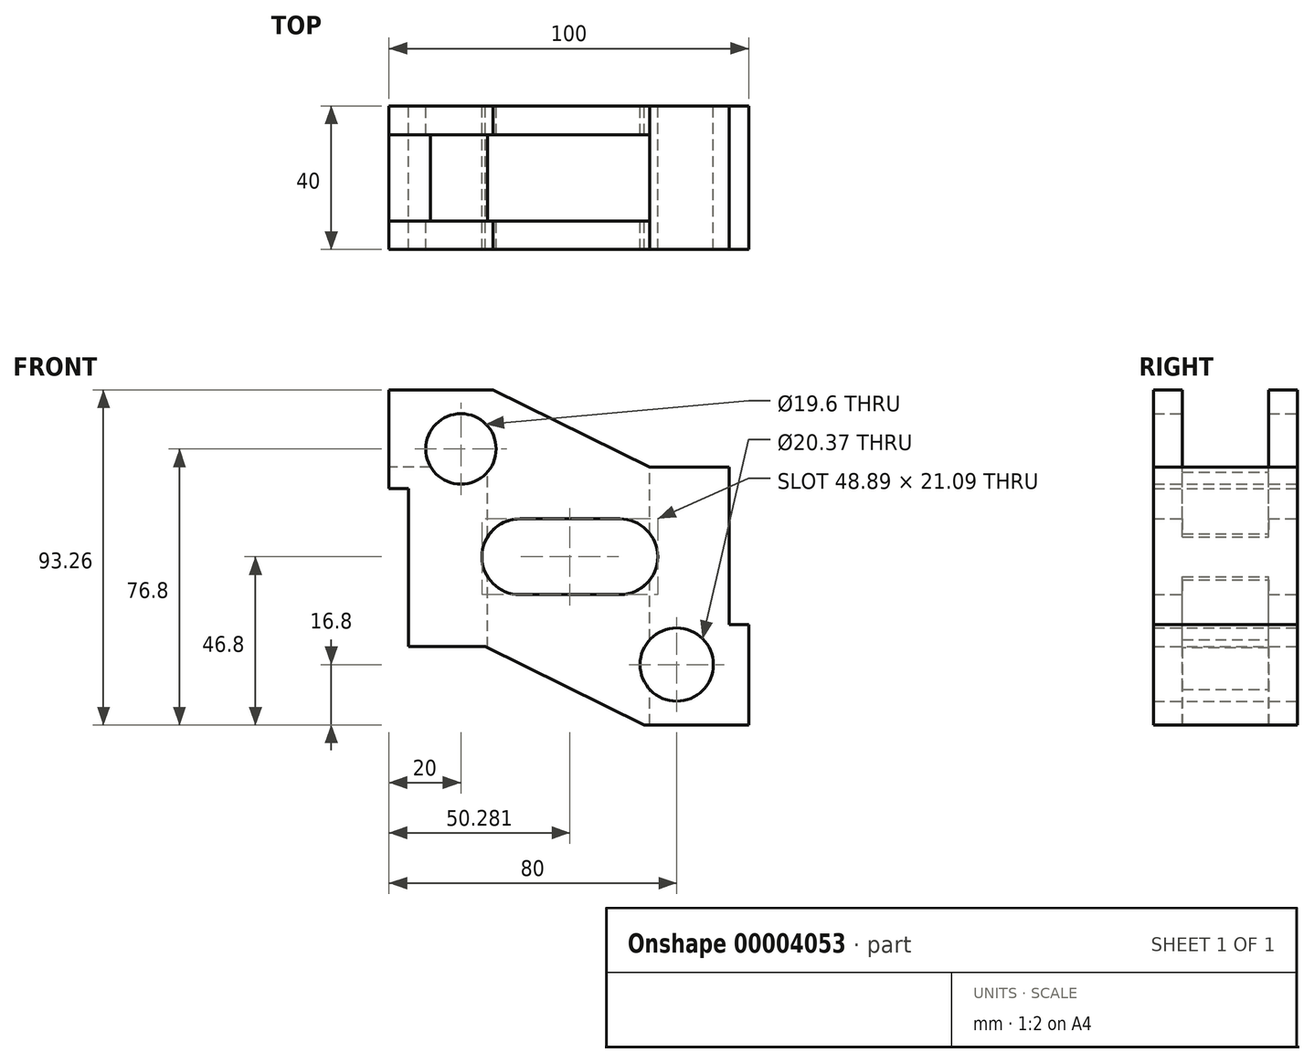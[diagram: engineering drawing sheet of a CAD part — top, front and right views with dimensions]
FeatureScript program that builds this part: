
annotation { "Feature Type Name" : "Feature", "Feature Type Description" : "" }
export const myFeature = defineFeature(function(context is Context, id is Id, definition is map)
    precondition{}
    {
        {
            var Q0;
            Q0=qCreatedBy(makeId("Front.planeOp"),FACE);
            var sketch = newSketch(context, id + "F0", { "sketchPlane" : qUnion([Q0])});
            skLineSegment(sketch, "E0", {"start": v(-50, 18.93) * mm, "end": v(-50, 46.46) * mm});
            skLineSegment(sketch, "E1", {"start": v(-50, 46.46) * mm, "end": v(-21.02, 46.46) * mm});
            skLineSegment(sketch, "E2", {"start": v(-21.02, 46.46) * mm, "end": v(22.51, 25) * mm});
            skLineSegment(sketch, "E3", {"start": v(22.51, 25) * mm, "end": v(44.58, 25) * mm});
            skLineSegment(sketch, "E4", {"start": v(50, -18.93) * mm, "end": v(50, -46.8) * mm});
            skLineSegment(sketch, "E5", {"start": v(50, -46.8) * mm, "end": v(21.02, -46.8) * mm});
            skLineSegment(sketch, "E6", {"start": v(21.02, -46.8) * mm, "end": v(-23.2, -25) * mm});
            skLineSegment(sketch, "E7", {"start": v(-23.2, -25) * mm, "end": v(-44.58, -25) * mm});
            skCircle(sketch, "E8", {"center": v(-30, 30) * mm, "radius": 9.8 * mm});
            skCircle(sketch, "E9", {"center": v(30, -30) * mm, "radius": 10.19 * mm});
            skLineSegment(sketch, "E10", {"start": v(-50, 18.93) * mm, "end": v(-44.58, 18.93) * mm});
            skLineSegment(sketch, "E11", {"start": v(-44.58, 18.93) * mm, "end": v(-44.58, -25) * mm});
            skLineSegment(sketch, "E12", {"start": v(44.58, 25) * mm, "end": v(44.58, -18.93) * mm});
            skLineSegment(sketch, "E13", {"start": v(44.58, -18.93) * mm, "end": v(50, -18.93) * mm});
            skArc(sketch, "E14", {"start": v(-13.62, 10.55) * mm, "mid": v(-24.16, 0) * mm, "end": v(-13.62, -10.55) * mm});
            skArc(sketch, "E15", {"start": v(14.18, -10.55) * mm, "mid": v(24.72, 0) * mm, "end": v(14.18, 10.55) * mm});
            skLineSegment(sketch, "E16", {"start": v(-13.62, 10.55) * mm, "end": v(14.18, 10.55) * mm});
            skLineSegment(sketch, "E17", {"start": v(-13.62, -10.55) * mm, "end": v(14.18, -10.55) * mm});
            skSolve(sketch);
        }
        {
            var Q0;
            Q0 = qSketchRegion(id + "F0", true);
            extrude(context, id + "F1", {"entities" : qUnion([Q0]), "endBound" : BoundingType.SYMMETRIC, "depth" : 40 * mm});
        }
        {
            var Q0;
            Q0=makeQuery(id+"F1.opExtrude","SWEPT_FACE",FACE,{"disambiguationData":[OSD([sQuery(id+"F0.wireOp",EDGE,"E3")])]});
            var sketch = newSketch(context, id + "F2", { "sketchPlane" : qUnion([Q0])});
            skLineSegment(sketch, "E18.bottom", {"start": v(44.58, -12) * mm, "end": v(-67.73, -12) * mm});
            skLineSegment(sketch, "E18.top", {"start": v(44.58, 12) * mm, "end": v(-67.73, 12) * mm});
            skLineSegment(sketch, "E18.left", {"start": v(44.58, -12) * mm, "end": v(44.58, 12) * mm});
            skLineSegment(sketch, "E18.right", {"start": v(-67.73, -12) * mm, "end": v(-67.73, 12) * mm});
            skSolve(sketch);
        }
        {
            var Q0;
            Q0 = qSketchRegion(id + "F2", true);
            var Q1;
            Q1=makeQuery(id+"F1.opExtrude","SWEPT_FACE",FACE,{"disambiguationData":[OSD([sQuery(id+"F0.wireOp",EDGE,"E1")])]});
            extrude(context, id + "F3", {"entities" : qUnion([Q0]), "operationType" : NewBodyOperationType.REMOVE, "endBound" : BoundingType.UP_TO_SURFACE, "endBoundEntityFace" : qUnion([Q1]), "depth" : 45.82 * mm});
        }
        {
            var Q0;
            Q0=makeQuery(id+"F3.boolean.opBoolean","MERGE",FACE,{"derivedFrom":[makeQuery(id+"F1.opExtrude","SWEPT_FACE",FACE,{"disambiguationData":[OSD([sQuery(id+"F0.wireOp",EDGE,"E3")])]}),makeQuery(id+"F3.opExtrude","CAP_FACE",FACE,{"disambiguationData":[OSD([sQuery(id+"F2.wireOp",EDGE,"E18.bottom"),sQuery(id+"F2.wireOp",EDGE,"E18.top"),sQuery(id+"F2.wireOp",EDGE,"E18.left"),sQuery(id+"F2.wireOp",EDGE,"E18.right")])],"isStart":true})]});
            var sketch = newSketch(context, id + "F4", { "sketchPlane" : qUnion([Q0])});
            skLineSegment(sketch, "E19.bottom", {"start": v(22.51, -12) * mm, "end": v(-22.58, -12) * mm});
            skLineSegment(sketch, "E19.top", {"start": v(22.51, 12) * mm, "end": v(-22.58, 12) * mm});
            skLineSegment(sketch, "E19.left", {"start": v(22.51, -12) * mm, "end": v(22.51, 12) * mm});
            skLineSegment(sketch, "E19.right", {"start": v(-22.58, -12) * mm, "end": v(-22.58, 12) * mm});
            skSolve(sketch);
        }
        {
            var Q0;
            Q0 = qSketchRegion(id + "F4", true);
            extrude(context, id + "F5", {"entities" : qUnion([Q0]), "operationType" : NewBodyOperationType.REMOVE, "oppositeDirection" : true, "depth" : 91.3 * mm});
        }
    });
